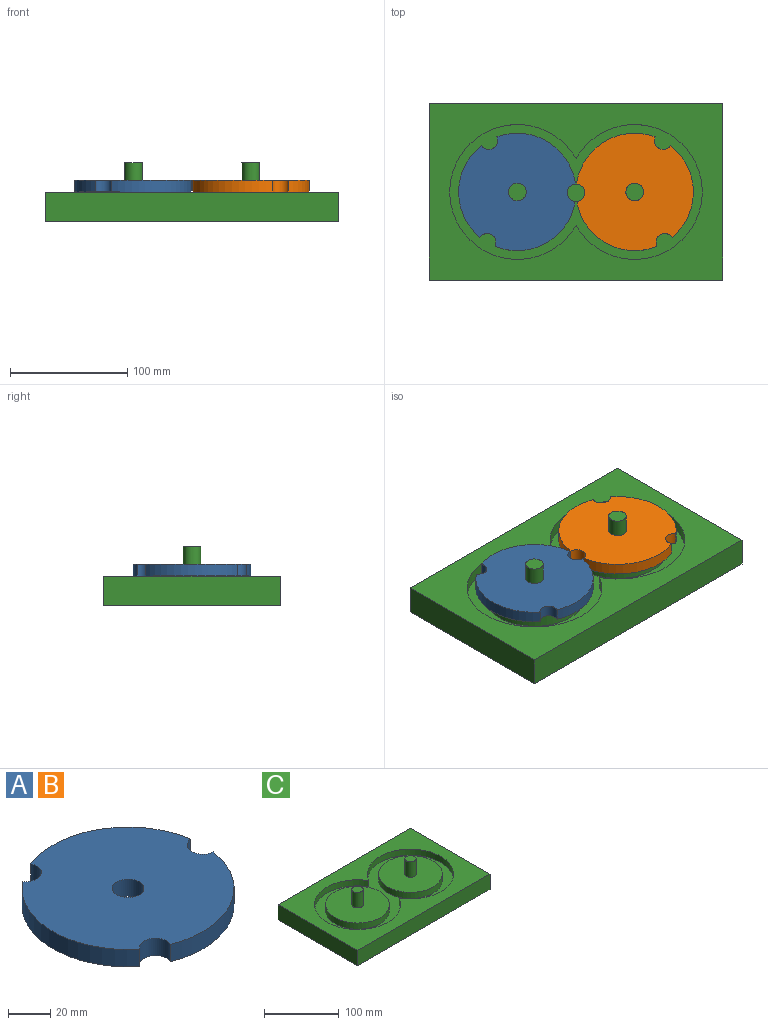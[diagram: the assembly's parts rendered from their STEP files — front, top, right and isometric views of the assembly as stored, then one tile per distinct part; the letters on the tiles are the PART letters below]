
ASSEMBLY  parts=3 mates=2
PART A: 9 faces, bbox 99.4x100x10 mm
  f0: cylinder r=7.5mm len=13.7mm, axis (0,0,-1), area 224.4mm2, adj f1,f6,f7,f8
  f1: cylinder r=50mm len=67.68mm, axis (0,0,-1), area 897.1mm2, adj f0,f2,f7,f8
  f2: cylinder r=7.5mm len=14.96mm, axis (0,0,-1), area 224.4mm2, adj f1,f3,f7,f8
  f3: cylinder r=50mm len=67.68mm, axis (0,0,-1), area 897.1mm2, adj f2,f4,f7,f8
  f4: cylinder r=7.5mm len=13.7mm, axis (0,0,-1), area 224.4mm2, adj f3,f6,f7,f8
  f5: cylinder r=7.5mm len=15mm, axis (0,0,-1), area 471.2mm2, adj f7,f8
  f6: cylinder r=50mm len=78.15mm, axis (0,0,-1), area 897.1mm2, adj f0,f4,f7,f8
  f7: plane 100x99.44mm, normal (0,0,1), area 7420.6mm2, adj f0,f1,f2,f3,f4,f5,f6
  f8: plane 100x99.44mm, normal (0,0,-1), area 7420.6mm2, adj f0,f1,f2,f3,f4,f5,f6
PART B: same geometry as A
PART C: 17 faces, bbox 250x150x50 mm
  f0: plane 85x85mm, normal (0,0,1), area 5497.8mm2, adj f1,f4
  f1: cylinder r=7.5mm len=25mm, axis (0,0,-1), area 1178.1mm2, adj f0,f2
  f2: plane 15x15mm, normal (0,0,1), area 176.7mm2, adj f1
  f3: cylinder r=57.5mm len=115mm, axis (0,0,1), area 3018.9mm2, adj f5,f7,f13
  f4: cylinder r=42.5mm len=85mm, axis (0,0,1), area 2670.4mm2, adj f0,f7
  f5: cylinder r=57.5mm len=115mm, axis (0,0,1), area 3018.9mm2, adj f3,f7,f13
  f6: cylinder r=42.5mm len=85mm, axis (0,0,1), area 2670.4mm2, adj f7,f16
  f7: plane 215x115mm, normal (0,0,1), area 8849mm2, adj f3,f4,f5,f6
  f8: plane 250x150mm, normal (0,0,-1), area 37500mm2, adj f9,f10,f11,f12
  f9: plane 150x25mm, normal (1,0,0), area 3750mm2, adj f8,f10,f12,f13
  f10: plane 250x25mm, normal (0,-1,0), area 6250mm2, adj f8,f9,f11,f13
  f11: plane 150x25mm, normal (-1,0,0), area 3750mm2, adj f8,f10,f12,f13
  f12: plane 250x25mm, normal (0,1,0), area 6250mm2, adj f8,f9,f11,f13
  f13: plane 250x150mm, normal (0,0,1), area 17302mm2, adj f3,f5,f9,f10,f11,f12
  f14: plane 15x15mm, normal (0,0,1), area 176.7mm2, adj f15
  f15: cylinder r=7.5mm len=25mm, axis (0,0,-1), area 1178.1mm2, adj f14,f16
  f16: plane 85x85mm, normal (0,0,1), area 5497.8mm2, adj f6,f15
PLACE A rot(axis=(0,0,-1),0.9deg) t=(-50,0,25)mm
PLACE B rot(axis=(0,0,-1),179.1deg) t=(50,0,25)mm
PLACE C t=(-125,75,0)mm
MATE revolute A.f1 <-> C.f1  axis (0,0,-1) through (-50,0,25)mm
MATE revolute B.f5 <-> C.f5  axis (0,0,-1) through (50,0,25)mm
